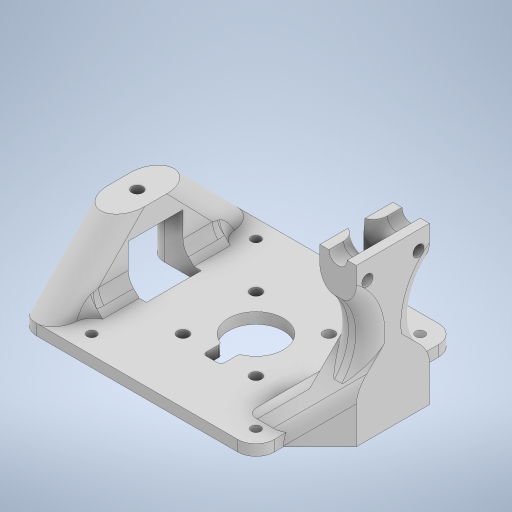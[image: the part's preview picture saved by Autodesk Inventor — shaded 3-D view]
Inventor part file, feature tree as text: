
AUTODESK INVENTOR PART (.ipt)
format: ipt  version: 2023 (Build 270158000, 158)  size: 577,536 bytes
history: native  units: in
note: dims shown in document units (in); Inventor stores cm internally (conversion verified against a paired STEP export)
features: extrude x9, sketch x9, chamfer x5, fillet x4
ambient origin geometry x8: Origin, YZ Plane, XZ Plane, XY Plane, X Axis, Y Axis, Z Axis, Center Point
bodies: Solid1 (feature_tree)
feature tree (27):
  extrude  "Extrusion1"  Depth=1.7717in
  extrude  "Extrusion3"  Depth=0.0984in
  extrude  "Extrusion4"  Depth=0.0984in
  extrude  "Extrusion5"  Depth=0.7874in
  chamfer  "Chamfer5"  Distance=0.1181in
  chamfer  "Chamfer6"  Distance=2.1654in
  extrude  "Extrusion6"  Depth=2.1654in
  extrude  "Extrusion7"  Depth=0.1969in
  extrude  "Extrusion8"  Depth=0.1969in
  extrude  "Extrusion9"  Depth=0.1181in TaperAngle=0.0deg
  fillet  "Fillet1"  Radius=0.5906in
  chamfer  "Chamfer8"  Distance=0.3937in
  chamfer  "Chamfer9"  Distance=0.3937in
  chamfer  "Chamfer10"  Distance=0.1969in
  extrude  "Extrusion10"  Depth=0.1969in
  fillet  "Fillet3"  Radius=0.1969in
  fillet  "Fillet4"  Radius=0.0394in
  fillet  "Fillet5"  Radius=0.2953in
  sketch  "Sketch1"  dims[d0=1.7717in d1=1.7717in]
  sketch  "Sketch3"  dims[d2=0.0984in d3=0.0984in]
  sketch  "Sketch4"  dims[d4=0.0984in d5=0.0984in]
  sketch  "Sketch5"  dims[d6=0.7874in d7=0.7874in]
  sketch  "Sketch6"  dims[d8=0.4921in]
  sketch  "Sketch7"  dims[d9=0.4921in]
  sketch  "Sketch8"  dims[d10=0.1181in]
  sketch  "Sketch9"  dims[d11=0.1181in]
  sketch  "Sketch10"  dims[d12=0.1181in d13=0.1181in d14=2.1654in d15=2.1654in d16=0.1969in d17=0.1969in d22=0.1181in d23=0.0in d24=0.5906in d27=0.3937in d28=0.3937in d29=0.1969in d30=0.1969in d31=0.1969in d32=0.0394in d33=0.2953in d34=0.3937in d35=0.7874in d52=0.3937in d53=0.5906in d54=0.7874in d55=0.2362in d58=0.5906in d59=0.2953in d60=0.3937in d61=0.0in d62=0.1181in d63=0.3937in d64=0.0in d65=0.5906in d66=0.5906in d67=0.0in d68=0.1181in d69=0.0787in d70=45.0deg d71=0.0in d72=0.3937in d73=0.3937in d74=0.1181in d75=0.0787in d76=45.0deg d77=0.3937in d78=0.3937in d79=0.0in d80=1.5748in d81=0.0in d82=0.1969in d83=1.5748in d84=0.0in d85=0.1969in d86=0.1181in d87=0.5512in d88=0.1181in d89=0.1181in d90=0.3937in d91=0.0in d95=0.315in d96=0.1575in d97=0.2953in d98=0.0in d99=0.1575in d100=0.3937in d101=0.0787in d102=45.0deg d103=0.3937in d104=0.0787in d105=45.0deg d106=0.3937in d107=0.0787in d108=45.0deg d110=0.7874in d111=0.5906in d112=0.5906in d113=0.2953in d114=0.0in d115=0.1575in d116=0.1969in d117=0.1969in d38=0.0197in d39=0.0344in d40=0.0197in d41=0.0344in d109=0.0in]
